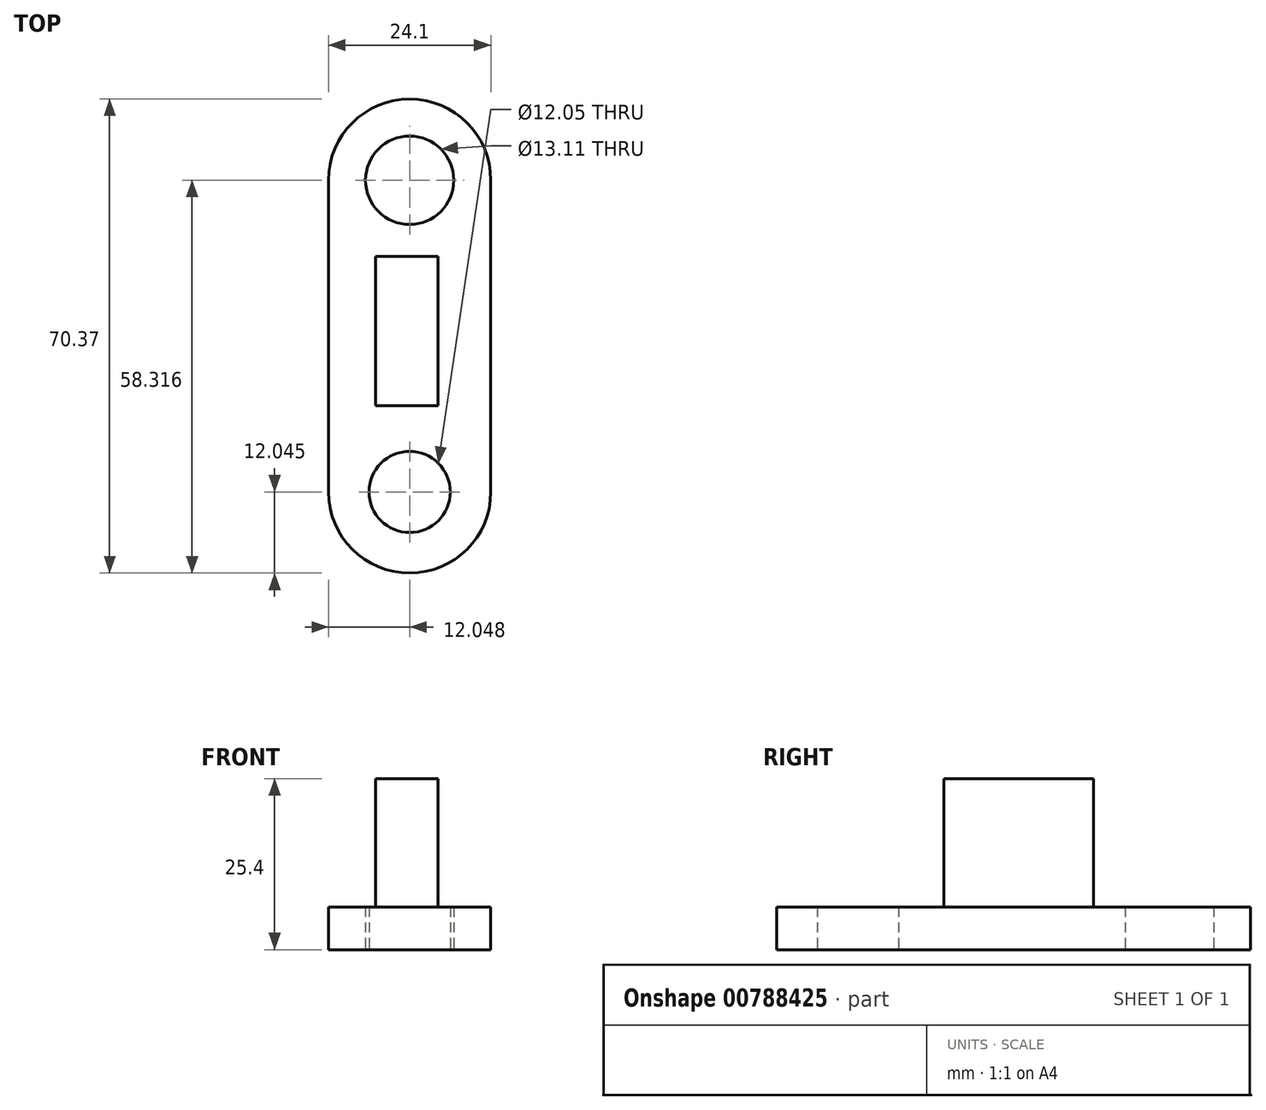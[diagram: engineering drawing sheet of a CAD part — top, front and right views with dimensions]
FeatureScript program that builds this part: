
annotation { "Feature Type Name" : "Feature", "Feature Type Description" : "" }
export const myFeature = defineFeature(function(context is Context, id is Id, definition is map)
    precondition{}
    {
        {
            var Q0;
            Q0=qCreatedBy(makeId("Top.planeOp"),FACE);
            var sketch = newSketch(context, id + "F0", { "sketchPlane" : qUnion([Q0])});
            skLineSegment(sketch, "E0", {"start": v(-36.75, 25.67) * mm, "end": v(-36.75, -20.6) * mm});
            skLineSegment(sketch, "E1", {"start": v(-12.65, 25.67) * mm, "end": v(-12.65, -20.6) * mm});
            skArc(sketch, "E2", {"start": v(-36.75, -20.6) * mm, "mid": v(-24.7, -32.65) * mm, "end": v(-12.65, -20.6) * mm});
            skArc(sketch, "E3", {"start": v(-12.65, 25.67) * mm, "mid": v(-24.7, 37.72) * mm, "end": v(-36.75, 25.67) * mm});
            skCircle(sketch, "E4", {"center": v(-24.7, -20.6) * mm, "radius": 6.02 * mm});
            skCircle(sketch, "E5", {"center": v(-24.7, 25.67) * mm, "radius": 6.56 * mm});
            skLineSegment(sketch, "E6.bottom", {"start": v(-20.5, 14.37) * mm, "end": v(-29.78, 14.37) * mm});
            skLineSegment(sketch, "E6.top", {"start": v(-20.5, -7.81) * mm, "end": v(-29.78, -7.81) * mm});
            skLineSegment(sketch, "E6.left", {"start": v(-20.5, 14.37) * mm, "end": v(-20.5, -7.81) * mm});
            skLineSegment(sketch, "E6.right", {"start": v(-29.78, 14.37) * mm, "end": v(-29.78, -7.81) * mm});
            skPoint(sketch, "E6.middle", {"position": v(-25.14, 3.28) * mm});
            skLineSegment(sketch, "E7", {"start": v(-25.14, -7.81) * mm, "end": v(-25.14, 14.37) * mm});
            skSolve(sketch);
        }
        {
            var Q0;
            Q0 = qSketchRegion(id + "F0", true);
            extrude(context, id + "F1", {"entities" : qUnion([Q0]), "depth" : 6.35 * mm, "offsetDistance" : 25.4 * mm});
        }
        {
            var Q0;
            Q0=makeQuery(id+"F0.imprint","IMPRINT",FACE,{"disambiguationData":[TD([[makeQuery(id+"F0.imprint","IMPRINT",EDGE,{"derivedFrom":sQuery(id+"F0.wireOp",EDGE,"E6.bottom")}),1.0]])]});
            extrude(context, id + "F2", {"entities" : qUnion([Q0]), "operationType" : NewBodyOperationType.ADD, "depth" : 25.4 * mm, "offsetDistance" : 25.4 * mm});
        }
    });
